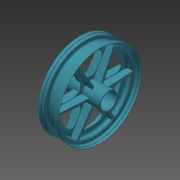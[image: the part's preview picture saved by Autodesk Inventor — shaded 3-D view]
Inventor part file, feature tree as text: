
AUTODESK INVENTOR PART (.ipt)
format: ipt  version: 2015 (Build 190159000, 159)  size: 626,688 bytes
history: native  units: mm
features: other x7, sketch x5, extrude x2, revolve x1, hole x1, loft x1, pattern_circular x1
ambient origin geometry x8: Origin, YZ Plane, XZ Plane, XY Plane, X Axis, Y Axis, Z Axis, Center Point
bodies: Body1 (feature_tree)
feature tree (18):
  other  "Bryła1"
  revolve  "Obrót1"
  hole  "Otwór na oś"  [1 undecoded]
  extrude  "Wyciągnięcie zmniejszenie masy"  TaperAngle=60.0deg  [1 undecoded]
  other  "Płaszczyzna konstrukcyjna1"
  sketch  "Szkic6"
  loft  "Wyciągnięcie wzmocnienie"
  extrude  "Wyciągnięcie proste2"  Depth=2.5mm
  pattern_circular  "Szyk wzmocnień"  [2 undecoded]
  sketch  "Szkic1"
  sketch  "Szkic5"
  sketch  "Szkic8"
  sketch  "Szkic9"
  other  "Płaszczyzna konstrukcyjna3"
  other  "Płaszczyzna konstrukcyjna4"
  other  "Płaszczyzna konstrukcyjna5"
  other  "Płaszczyzna konstrukcyjna6"
  other  "Płaszczyzna konstrukcyjna7"
note: 4 required parameter values undecoded (feature->parameter linkage not recoverable at this tier; creation-order binding heuristic only, values carry confidence <= 0.55)
